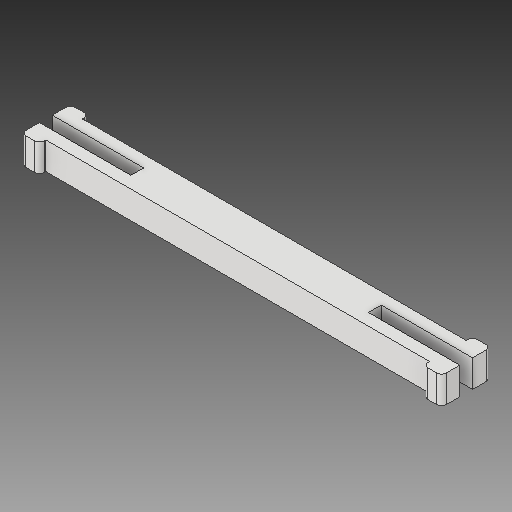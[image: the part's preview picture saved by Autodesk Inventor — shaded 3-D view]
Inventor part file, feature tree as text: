
AUTODESK INVENTOR PART (.ipt)
format: ipt  version: 2018 (Build 220112000, 112)  size: 135,168 bytes
history: native  units: mm
features: extrude x1, fillet x1, sketch x1
ambient origin geometry x8: Origin, YZ Plane, XZ Plane, XY Plane, X Axis, Y Axis, Z Axis, Center Point
bodies: Solid1 (feature_tree)
feature tree (3):
  extrude  "Extrusion1"  Depth=2.0mm
  fillet  "Fillet1"  Radius=0.7mm
  sketch  "Sketch1"  dims[d0=23.0mm d1=2.0mm d2=0.7mm d3=10.0mm d4=0.7mm d5=2.0mm d6=3.0mm d7=0.0mm d8=0.5mm]
